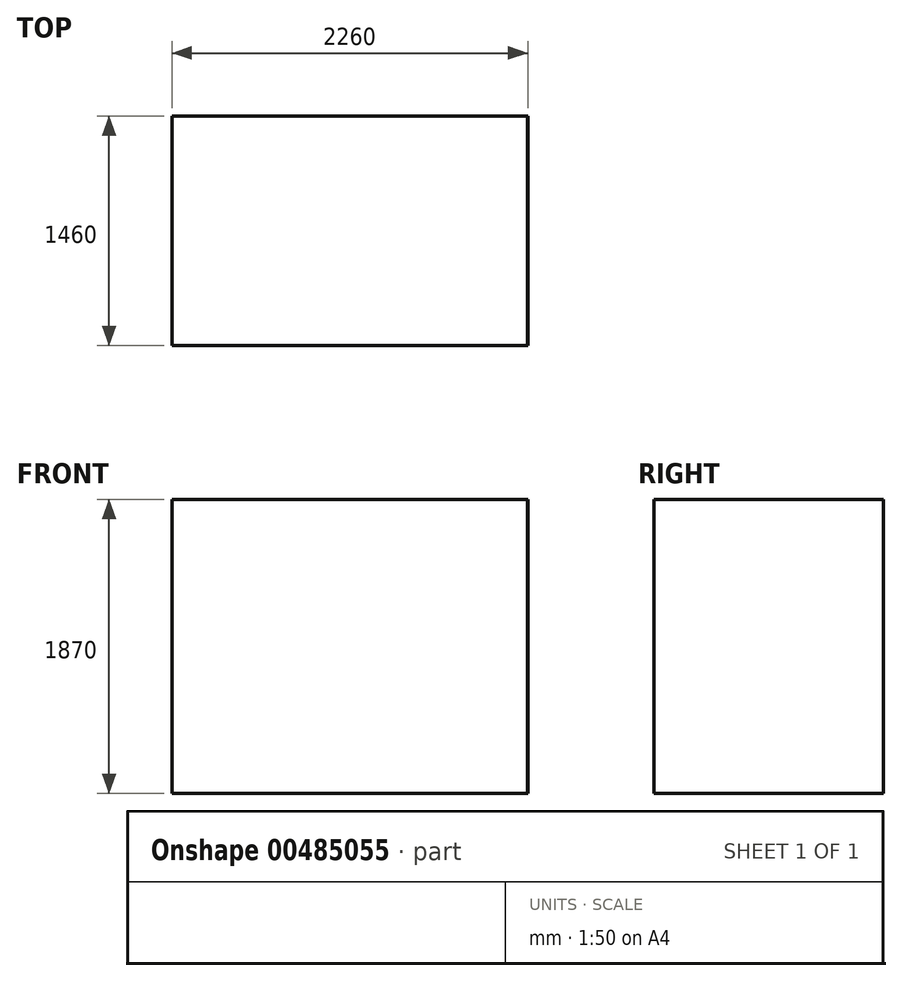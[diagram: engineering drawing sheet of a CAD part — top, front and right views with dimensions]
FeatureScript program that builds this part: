
annotation { "Feature Type Name" : "Feature", "Feature Type Description" : "" }
export const myFeature = defineFeature(function(context is Context, id is Id, definition is map)
    precondition{}
    {
        {
            var Q0;
            Q0=qCreatedBy(makeId("Top.planeOp"),FACE);
            var sketch = newSketch(context, id + "F0", { "sketchPlane" : qUnion([Q0])});
            skLineSegment(sketch, "E0.bottom", {"start": v(1130, 730) * mm, "end": v(-1130, 730) * mm});
            skLineSegment(sketch, "E0.top", {"start": v(1130, -730) * mm, "end": v(-1130, -730) * mm});
            skLineSegment(sketch, "E0.left", {"start": v(1130, 730) * mm, "end": v(1130, -730) * mm});
            skLineSegment(sketch, "E0.right", {"start": v(-1130, 730) * mm, "end": v(-1130, -730) * mm});
            skPoint(sketch, "E0.middle", {"position": v(0, 0) * mm});
            skSolve(sketch);
        }
        {
            var Q0;
            Q0=qSketchRegion(id+"F0",true);
            extrude(context, id + "F1", {"entities" : qUnion([Q0]), "depth" : 1870 * mm, "offsetDistance" : 25 * mm});
        }
        {
            var Q0;
            Q0=makeQuery(id+"F1.opExtrude","CAP_FACE",FACE,{"disambiguationData":[OSD([sQuery(id+"F0.wireOp",EDGE,"E0.bottom"),sQuery(id+"F0.wireOp",EDGE,"E0.top"),sQuery(id+"F0.wireOp",EDGE,"E0.left"),sQuery(id+"F0.wireOp",EDGE,"E0.right")])],"isStart":false});
            var Q1;
            Q1=makeQuery(id+"F1.opExtrude","SWEPT_FACE",FACE,{"disambiguationData":[OSD([sQuery(id+"F0.wireOp",EDGE,"E0.top")])]});
            shell(context, id + "F2", {"entities" : qUnion([Q0, Q1]), "thickness" : 1 * mm});
        }
    });
